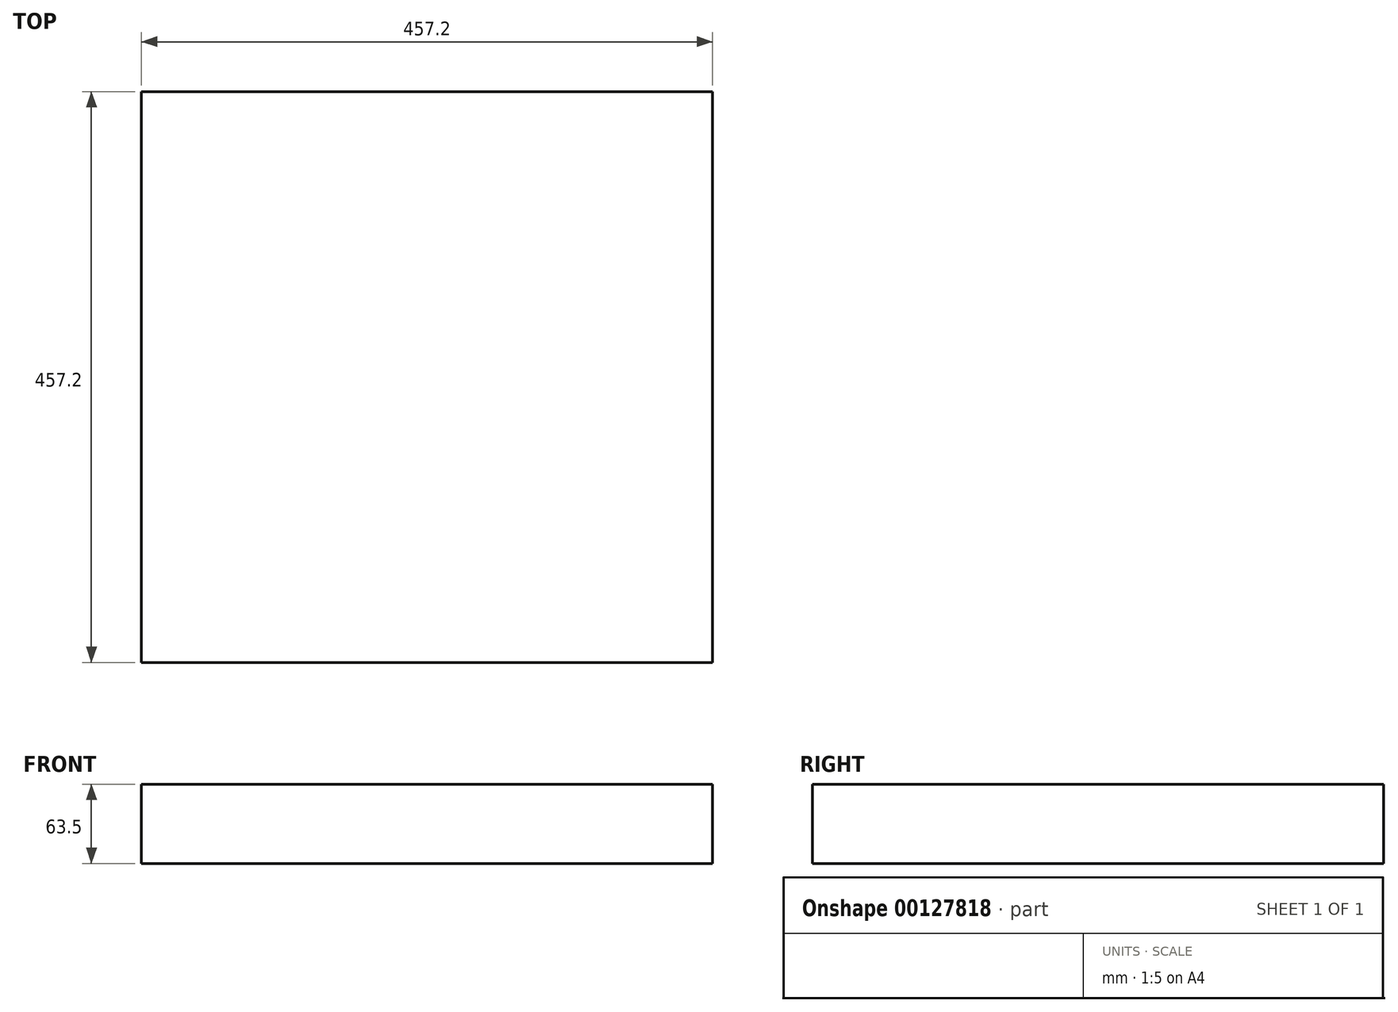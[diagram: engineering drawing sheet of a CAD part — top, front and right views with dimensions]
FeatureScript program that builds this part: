
annotation { "Feature Type Name" : "Feature", "Feature Type Description" : "" }
export const myFeature = defineFeature(function(context is Context, id is Id, definition is map)
    precondition{}
    {
        {
            var Q0;
            Q0=qCreatedBy(makeId("Top.planeOp"),FACE);
            var sketch = newSketch(context, id + "F0", { "sketchPlane" : qUnion([Q0])});
            skLineSegment(sketch, "E0.bottom", {"start": v(0, 0) * mm, "end": v(457.2, 0) * mm});
            skLineSegment(sketch, "E0.top", {"start": v(0, -457.2) * mm, "end": v(457.2, -457.2) * mm});
            skLineSegment(sketch, "E0.left", {"start": v(0, 0) * mm, "end": v(0, -457.2) * mm});
            skLineSegment(sketch, "E0.right", {"start": v(457.2, 0) * mm, "end": v(457.2, -457.2) * mm});
            skSolve(sketch);
        }
        {
            var Q0;
            Q0 = qSketchRegion(id + "F0", true);
            extrude(context, id + "F1", {"entities" : qUnion([Q0]), "depth" : 63.5 * mm});
        }
    });
